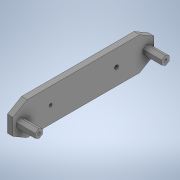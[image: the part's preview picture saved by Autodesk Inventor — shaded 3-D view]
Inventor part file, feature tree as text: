
AUTODESK INVENTOR PART (.ipt)
format: ipt  version: 2020 (Build 240168000, 168)  size: 221,696 bytes
history: native  units: in
note: dims shown in document units (in); Inventor stores cm internally (conversion verified against a paired STEP export)
features: extrude x7, sketch x7, plane x1
ambient origin geometry x8: Origin, YZ Plane, XZ Plane, XY Plane, X Axis, Y Axis, Z Axis, Center Point
bodies: Solid1 (feature_tree)
feature tree (15):
  extrude  "Extrusion1"  Depth=5.9055in
  extrude  "Extrusion3"  TaperAngle=0.0deg  [1 undecoded]
  extrude  "Extrusion4"  Depth=0.7874in
  plane  "Work Plane1"
  extrude  "Extrusion5"  Depth=0.122in
  extrude  "Extrusion6"  Depth=0.2402in
  extrude  "Extrusion7"  [1 undecoded]
  extrude  "Extrusion8"  Depth=0.0866in TaperAngle=0.0deg
  sketch  "Sketch1"  dims[d0=1.378in d1=5.9055in]
  sketch  "Sketch2"  dims[d2=0.2362in d3=0.0in]
  sketch  "Sketch3"  dims[d8=0.315in d9=0.7874in]
  sketch  "Sketch4"  dims[d10=0.0in d12=0.122in]
  sketch  "Sketch5"  dims[d13=0.0in d14=0.0in d15=0.2402in]
  sketch  "Sketch8"  dims[d16=0.0866in d17=-0.2233in]
  sketch  "Sketch9"  dims[d18=-0.3937in d19=0.0866in d20=0.0in d26=1.5748in d27=0.1654in d28=0.122in d29=1.5748in d30=0.0in d31=0.0in d32=0.2402in d33=0.0866in d34=-0.2233in]
note: 2 required parameter values undecoded (feature->parameter linkage not recoverable at this tier; creation-order binding heuristic only, values carry confidence <= 0.55)
